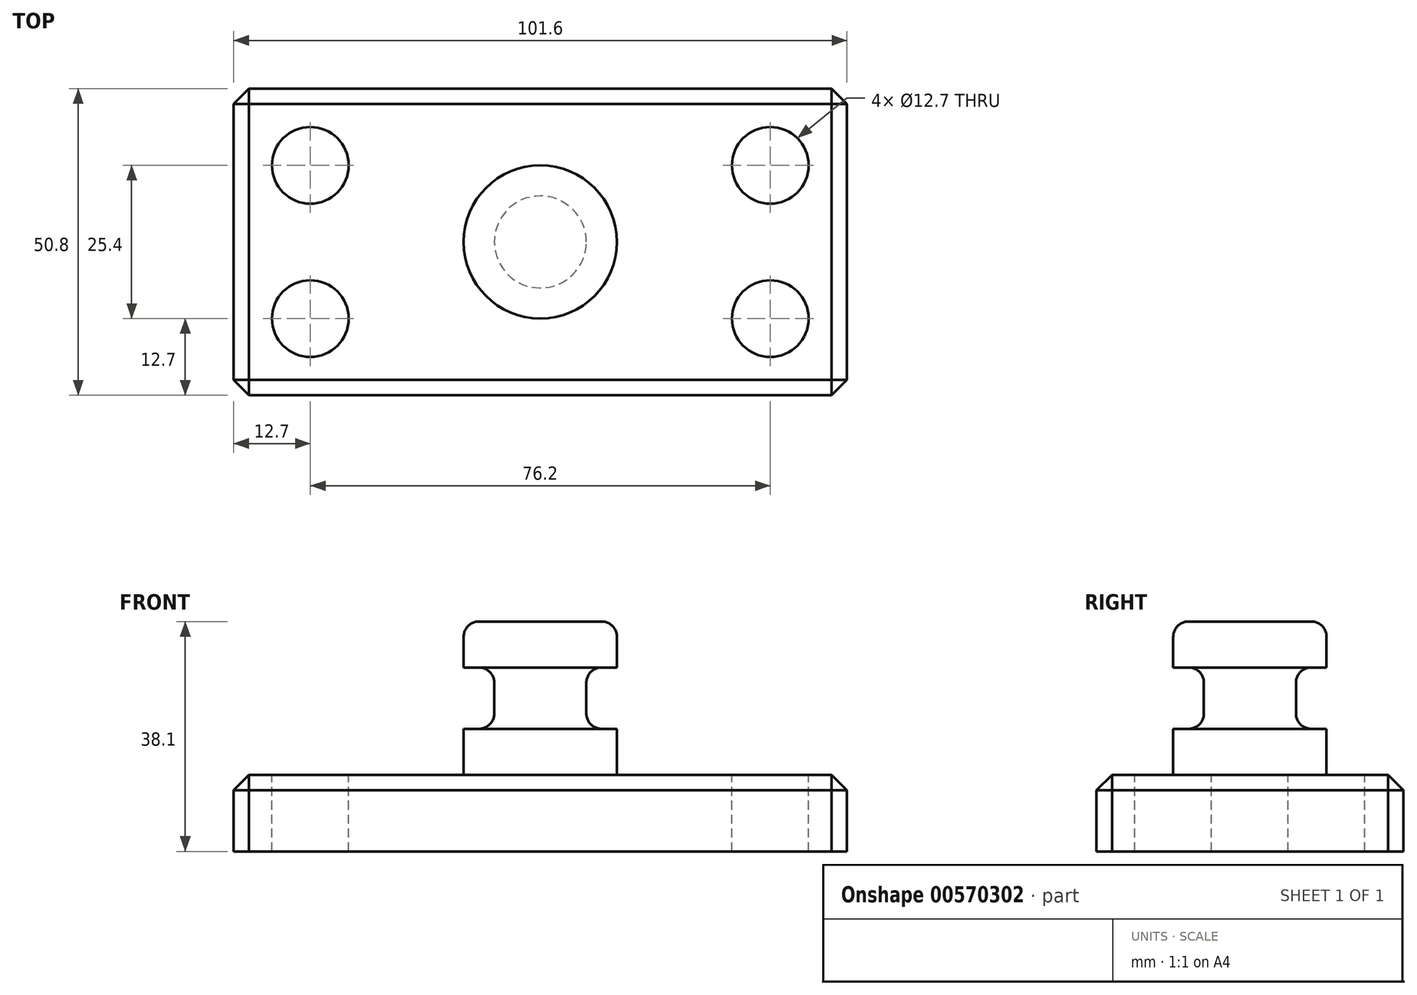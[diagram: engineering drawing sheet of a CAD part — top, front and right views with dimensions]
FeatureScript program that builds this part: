
annotation { "Feature Type Name" : "Feature", "Feature Type Description" : "" }
export const myFeature = defineFeature(function(context is Context, id is Id, definition is map)
    precondition{}
    {
        {
            var Q0;
            Q0=qCreatedBy(makeId("Top.planeOp"),FACE);
            var sketch = newSketch(context, id + "F0", { "sketchPlane" : qUnion([Q0])});
            skLineSegment(sketch, "E0.bottom", {"start": v(-50.8, 25.4) * mm, "end": v(50.8, 25.4) * mm});
            skLineSegment(sketch, "E0.top", {"start": v(-50.8, -25.4) * mm, "end": v(50.8, -25.4) * mm});
            skLineSegment(sketch, "E0.left", {"start": v(-50.8, 25.4) * mm, "end": v(-50.8, -25.4) * mm});
            skLineSegment(sketch, "E0.right", {"start": v(50.8, 25.4) * mm, "end": v(50.8, -25.4) * mm});
            skPoint(sketch, "E0.middle", {"position": v(0, 0) * mm});
            skSolve(sketch);
        }
        {
            var Q0;
            Q0 = qSketchRegion(id + "F0", true);
            extrude(context, id + "F1", {"entities" : qUnion([Q0]), "depth" : 12.7 * mm, "offsetDistance" : 25.4 * mm});
        }
        {
            var Q0;
            Q0=makeQuery(id+"F1.opExtrude","CAP_FACE",FACE,{"disambiguationData":[OSD([sQuery(id+"F0.wireOp",EDGE,"E0.bottom"),sQuery(id+"F0.wireOp",EDGE,"E0.top"),sQuery(id+"F0.wireOp",EDGE,"E0.left"),sQuery(id+"F0.wireOp",EDGE,"E0.right")])],"isStart":false});
            var sketch = newSketch(context, id + "F2", { "sketchPlane" : qUnion([Q0])});
            skCircle(sketch, "E1", {"center": v(-38.1, 12.7) * mm, "radius": 6.35 * mm});
            skCircle(sketch, "E2", {"center": v(38.1, 12.7) * mm, "radius": 6.35 * mm});
            skCircle(sketch, "E3", {"center": v(-38.1, -12.7) * mm, "radius": 6.35 * mm});
            skCircle(sketch, "E4", {"center": v(38.1, -12.7) * mm, "radius": 6.35 * mm});
            skSolve(sketch);
        }
        {
            var Q0;
            Q0 = qSketchRegion(id + "F2", true);
            extrude(context, id + "F3", {"entities" : qUnion([Q0]), "operationType" : NewBodyOperationType.REMOVE, "endBound" : BoundingType.THROUGH_ALL, "oppositeDirection" : true, "depth" : 25.4 * mm, "offsetDistance" : 25.4 * mm});
        }
        {
            var Q0;
            Q0=qCreatedBy(makeId("Front.planeOp"),FACE);
            var sketch = newSketch(context, id + "F4", { "sketchPlane" : qUnion([Q0])});
            skLineSegment(sketch, "E5.bottom", {"start": v(0, 12.7) * mm, "end": v(12.7, 12.7) * mm});
            skLineSegment(sketch, "E5.top", {"start": v(0, 38.1) * mm, "end": v(12.7, 38.1) * mm});
            skLineSegment(sketch, "E5.left", {"start": v(0, 12.7) * mm, "end": v(0, 38.1) * mm});
            skLineSegment(sketch, "E5.right", {"start": v(12.7, 12.7) * mm, "end": v(12.7, 38.1) * mm});
            skSolve(sketch);
        }
        {
            var Q0;
            Q0 = qSketchRegion(id + "F4", true);
            var Q1;
            Q1=sQuery(id+"F4.wireOp",EDGE,"E5.left");
            revolve(context, id + "F5", {"operationType" : NewBodyOperationType.ADD, "entities" : qUnion([Q0]), "axis" : qUnion([Q1]), "revolveType" : RevolveType.FULL});
        }
        {
            var Q0;
            Q0=qCreatedBy(makeId("Front.planeOp"),FACE);
            var sketch = newSketch(context, id + "F6", { "sketchPlane" : qUnion([Q0])});
            skLineSegment(sketch, "E6.bottom", {"start": v(7.62, 30.48) * mm, "end": v(12.7, 30.48) * mm});
            skLineSegment(sketch, "E6.top", {"start": v(7.62, 20.32) * mm, "end": v(12.7, 20.32) * mm});
            skLineSegment(sketch, "E6.left", {"start": v(12.7, 30.48) * mm, "end": v(12.7, 20.32) * mm});
            skLineSegment(sketch, "E6.right", {"start": v(7.62, 30.48) * mm, "end": v(7.62, 20.32) * mm});
            skSolve(sketch);
        }
        {
            var Q0;
            Q0 = qSketchRegion(id + "F6", true);
            var Q1;
            Q1=makeQuery(id+"F5.opRevolve","SWEPT_FACE",FACE,{"disambiguationData":[OSD([sQuery(id+"F4.wireOp",EDGE,"E5.right")])]});
            revolve(context, id + "F7", {"operationType" : NewBodyOperationType.REMOVE, "entities" : qUnion([Q0]), "axis" : qUnion([Q1]), "revolveType" : RevolveType.FULL, "oppositeDirection" : true});
        }
        {
            var Q0;
            Q0=makeQuery(id+"F5.opRevolve","SWEPT_FACE",FACE,{"disambiguationData":[OSD([sQuery(id+"F4.wireOp",EDGE,"E5.top")])]});
            var Q1;
            Q1=makeQuery(id+"F7.boolean.opBoolean","COPY",FACE,{"derivedFrom":makeQuery(id+"F7.opRevolve","SWEPT_FACE",FACE,{"disambiguationData":[OSD([sQuery(id+"F6.wireOp",EDGE,"E6.right")])]})});
            fillet(context, id + "F8", {"entities" : qUnion([Q0, Q1]), "radius" : 2.54 * mm, "tangentPropagation" : true, "allowEdgeOverflow" : false});
        }
        {
            var Q0;
            Q0=makeQuery(id+"F1.opExtrude","CAP_EDGE",EDGE,{"disambiguationData":[OSD([sQuery(id+"F0.wireOp",EDGE,"E0.top")])],"isStart":false});
            var Q1;
            Q1=makeQuery(id+"F1.opExtrude","CAP_EDGE",EDGE,{"disambiguationData":[OSD([sQuery(id+"F0.wireOp",EDGE,"E0.right")])],"isStart":false});
            var Q2;
            Q2=makeQuery(id+"F1.opExtrude","CAP_EDGE",EDGE,{"disambiguationData":[OSD([sQuery(id+"F0.wireOp",EDGE,"E0.bottom")])],"isStart":false});
            var Q3;
            Q3=makeQuery(id+"F1.opExtrude","CAP_EDGE",EDGE,{"disambiguationData":[OSD([sQuery(id+"F0.wireOp",EDGE,"E0.left")])],"isStart":false});
            var Q4;
            Q4=makeQuery(id+"F1.opExtrude","SWEPT_EDGE",EDGE,{"disambiguationData":[OSD([sQuery(id+"F0.wireOp",EDGE,"E0.top"),sQuery(id+"F0.wireOp",EDGE,"E0.right")])]});
            var Q5;
            Q5=makeQuery(id+"F1.opExtrude","SWEPT_EDGE",EDGE,{"disambiguationData":[OSD([sQuery(id+"F0.wireOp",EDGE,"E0.bottom"),sQuery(id+"F0.wireOp",EDGE,"E0.right")])]});
            var Q6;
            Q6=makeQuery(id+"F1.opExtrude","SWEPT_EDGE",EDGE,{"disambiguationData":[OSD([sQuery(id+"F0.wireOp",EDGE,"E0.top"),sQuery(id+"F0.wireOp",EDGE,"E0.left")])]});
            var Q7;
            Q7=makeQuery(id+"F1.opExtrude","SWEPT_EDGE",EDGE,{"disambiguationData":[OSD([sQuery(id+"F0.wireOp",EDGE,"E0.bottom"),sQuery(id+"F0.wireOp",EDGE,"E0.left")])]});
            chamfer(context, id + "F9", {"entities" : qUnion([Q0, Q1, Q2, Q3, Q4, Q5, Q6, Q7]), "width" : 2.54 * mm, "tangentPropagation" : true});
        }
    });
